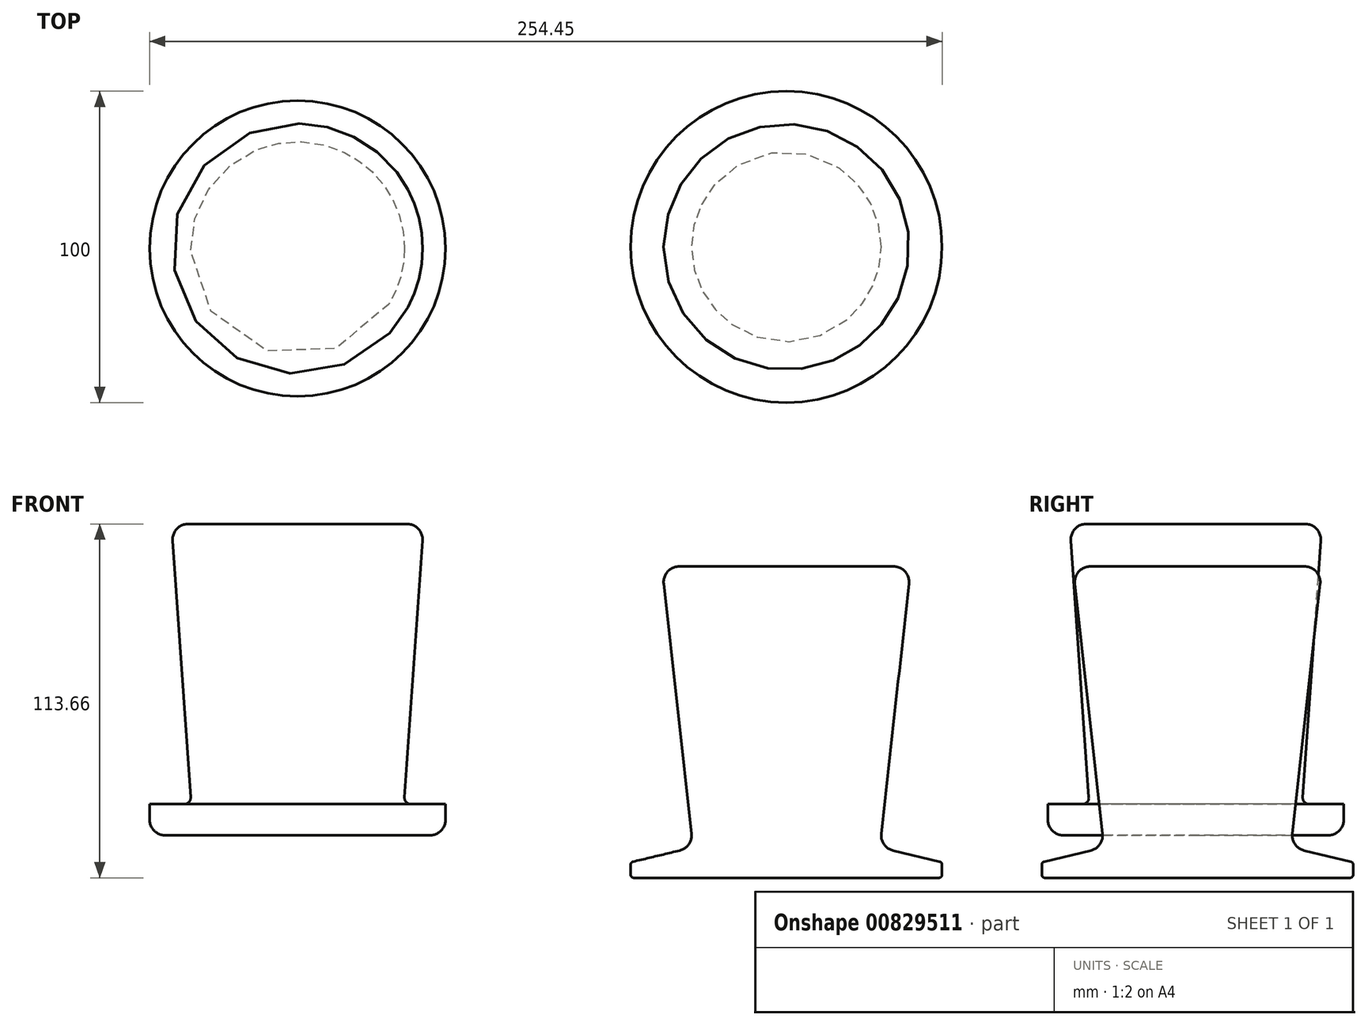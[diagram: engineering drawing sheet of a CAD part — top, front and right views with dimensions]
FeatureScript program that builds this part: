
annotation { "Feature Type Name" : "Feature", "Feature Type Description" : "" }
export const myFeature = defineFeature(function(context is Context, id is Id, definition is map)
    precondition{}
    {
        {
            var Q0;
            Q0=qCreatedBy(makeId("Top.planeOp"),FACE);
            var sketch = newSketch(context, id + "F0", { "sketchPlane" : qUnion([Q0])});
            skCircle(sketch, "E0", {"center": v(-0.58, -0.54) * mm, "radius": 47.5 * mm});
            skCircle(sketch, "E1", {"center": v(-0.58, -0.54) * mm, "radius": 33.5 * mm});
            skSolve(sketch);
        }
        {
            var Q0;
            Q0=makeQuery(id+"F0.imprint","IMPRINT",FACE,{"disambiguationData":[TD([[makeQuery(id+"F0.imprint","IMPRINT",EDGE,{"derivedFrom":sQuery(id+"F0.wireOp",EDGE,"E1")}),1.0]])]});
            var Q1;
            Q1=makeQuery(id+"F0.imprint","IMPRINT",FACE,{"disambiguationData":[TD([[makeQuery(id+"F0.imprint","IMPRINT",EDGE,{"derivedFrom":sQuery(id+"F0.wireOp",EDGE,"E0")}),1.0]])]});
            extrude(context, id + "F1", {"entities" : qUnion([Q0, Q1]), "depth" : 10 * mm, "offsetDistance" : 25 * mm});
        }
        {
            var Q0;
            Q0=makeQuery(id+"F0.imprint","IMPRINT",FACE,{"disambiguationData":[TD([[makeQuery(id+"F0.imprint","IMPRINT",EDGE,{"derivedFrom":sQuery(id+"F0.wireOp",EDGE,"E1")}),1.0]])]});
            extrude(context, id + "F2", {"entities" : qUnion([Q0]), "operationType" : NewBodyOperationType.ADD, "depth" : 100 * mm, "offsetDistance" : 25 * mm, "hasDraft" : true, "draftAngle" : 4 * degree});
        }
        {
            var Q0;
            Q0=makeQuery(id+"F1.opExtrude","CAP_EDGE",EDGE,{"disambiguationData":[OSD([sQuery(id+"F0.wireOp",EDGE,"E0")])],"isStart":true});
            fillet(context, id + "F3", {"entities" : qUnion([Q0]), "radius" : 5 * mm, "tangentPropagation" : true, "allowEdgeOverflow" : false});
        }
        {
            var Q0;
            Q0=makeQuery(id+"F2.boolean.opBoolean","INTERSECT",EDGE,{"derivedFrom":[makeQuery(id+"F1.opExtrude","CAP_FACE",FACE,{"disambiguationData":[OSD([sQuery(id+"F0.wireOp",EDGE,"E0")])],"isStart":false}),makeQuery(id+"F2.opExtrude","SWEPT_FACE",FACE,{"disambiguationData":[OSD([sQuery(id+"F0.wireOp",EDGE,"E1")])]})]});
            fillet(context, id + "F4", {"entities" : qUnion([Q0]), "radius" : 2 * mm, "tangentPropagation" : true, "allowEdgeOverflow" : false});
        }
        {
            var Q0;
            Q0=makeQuery(id+"F2.opExtrude","CAP_EDGE",EDGE,{"disambiguationData":[OSD([sQuery(id+"F0.wireOp",EDGE,"E1")])],"isStart":false});
            fillet(context, id + "F5", {"entities" : qUnion([Q0]), "radius" : 5 * mm, "tangentPropagation" : true, "allowEdgeOverflow" : false});
        }
        {
            var Q0;
            Q0=qCreatedBy(makeId("Front.planeOp"),FACE);
            var sketch = newSketch(context, id + "F6", { "sketchPlane" : qUnion([Q0])});
            skLineSegment(sketch, "E2", {"start": v(156.37, 86.34) * mm, "end": v(156.37, -13.66) * mm});
            skLineSegment(sketch, "E3", {"start": v(126.37, -3.9) * mm, "end": v(116.37, 86.34) * mm});
            skLineSegment(sketch, "E4", {"start": v(116.37, 86.34) * mm, "end": v(156.37, 86.34) * mm});
            skLineSegment(sketch, "E5", {"start": v(106.37, -13.66) * mm, "end": v(106.37, -8.66) * mm});
            skLineSegment(sketch, "E6", {"start": v(106.37, -8.66) * mm, "end": v(126.37, -3.9) * mm});
            skLineSegment(sketch, "E7", {"start": v(156.37, -13.66) * mm, "end": v(106.37, -13.66) * mm});
            skLineSegment(sketch, "E8", {"start": v(126.37, -3.9) * mm, "end": v(156.37, -3.9) * mm, "construction": true});
            skSolve(sketch);
        }
        {
            var Q0;
            Q0=makeQuery(id+"F6.imprint","IMPRINT",FACE,{"disambiguationData":[TD([[makeQuery(id+"F6.imprint","IMPRINT",EDGE,{"derivedFrom":sQuery(id+"F6.wireOp",EDGE,"E2")}),-1.0]])]});
            var Q1;
            Q1=sQuery(id+"F6.wireOp",EDGE,"E2");
            revolve(context, id + "F7", {"surfaceOperationType" : NewSurfaceOperationType.NEW, "entities" : qUnion([Q0]), "axis" : qUnion([Q1]), "revolveType" : RevolveType.FULL});
        }
        {
            var Q0;
            Q0=makeQuery(id+"F7.opRevolve","SWEPT_EDGE",EDGE,{"disambiguationData":[OSD([sQuery(id+"F6.wireOp",EDGE,"E3"),sQuery(id+"F6.wireOp",EDGE,"E4")])]});
            var Q1;
            Q1=makeQuery(id+"F7.opRevolve","SWEPT_EDGE",EDGE,{"disambiguationData":[OSD([sQuery(id+"F6.wireOp",EDGE,"E3"),sQuery(id+"F6.wireOp",EDGE,"E6")])]});
            fillet(context, id + "F8", {"entities" : qUnion([Q0, Q1]), "radius" : 5 * mm, "tangentPropagation" : true, "allowEdgeOverflow" : false});
        }
        {
            var Q0;
            Q0=makeQuery(id+"F7.opRevolve","SWEPT_FACE",FACE,{"disambiguationData":[OSD([sQuery(id+"F6.wireOp",EDGE,"E5")])]});
            fillet(context, id + "F9", {"entities" : qUnion([Q0]), "radius" : 1 * mm, "tangentPropagation" : true, "allowEdgeOverflow" : false});
        }
    });
